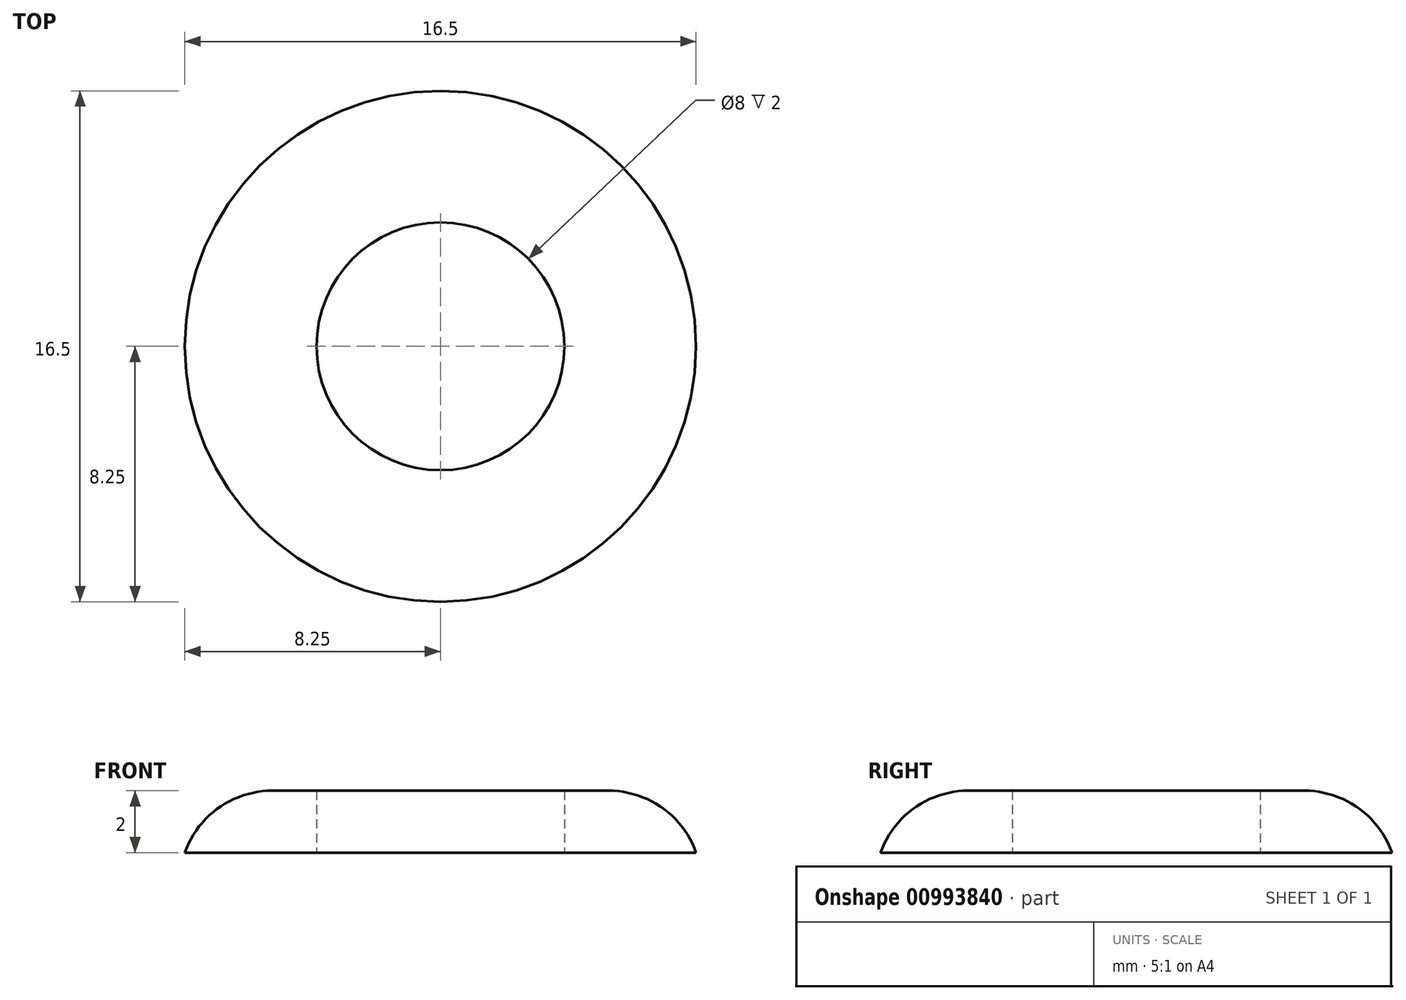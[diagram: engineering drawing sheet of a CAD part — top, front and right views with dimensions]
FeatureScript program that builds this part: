
annotation { "Feature Type Name" : "Feature", "Feature Type Description" : "" }
export const myFeature = defineFeature(function(context is Context, id is Id, definition is map)
    precondition{}
    {
        {
            var Q0;
            Q0=qCreatedBy(makeId("Top.planeOp"),FACE);
            var sketch = newSketch(context, id + "F0", { "sketchPlane" : qUnion([Q0])});
            skCircle(sketch, "E0", {"center": v(0, 0) * mm, "radius": 8.25 * mm});
            skCircle(sketch, "E1", {"center": v(0, 0) * mm, "radius": 4 * mm});
            skSolve(sketch);
        }
        {
            var Q0;
            Q0=makeQuery(id+"F0.imprint","IMPRINT",FACE,{"disambiguationData":[TD([[makeQuery(id+"F0.imprint","IMPRINT",EDGE,{"derivedFrom":sQuery(id+"F0.wireOp",EDGE,"E0")}),1.0]])]});
            var Q1;
            Q1=makeQuery(id+"F0.imprint","IMPRINT",FACE,{"disambiguationData":[TD([[makeQuery(id+"F0.imprint","IMPRINT",EDGE,{"derivedFrom":sQuery(id+"F0.wireOp",EDGE,"E1")}),1.0]])]});
            extrude(context, id + "F1", {"entities" : qUnion([Q0, Q1]), "depth" : 2 * mm, "offsetDistance" : 25 * mm});
        }
        {
            var Q0;
            Q0=makeQuery(id+"F0.imprint","IMPRINT",FACE,{"disambiguationData":[TD([[makeQuery(id+"F0.imprint","IMPRINT",EDGE,{"derivedFrom":sQuery(id+"F0.wireOp",EDGE,"E1")}),1.0]])]});
            var Q1;
            Q1=makeQuery(id+"F1.opExtrude","CAP_FACE",FACE,{"disambiguationData":[OSD([sQuery(id+"F0.wireOp",EDGE,"E0")])],"isStart":false});
            extrude(context, id + "F2", {"entities" : qUnion([Q0]), "operationType" : NewBodyOperationType.REMOVE, "endBound" : BoundingType.UP_TO_SURFACE, "depth" : 25 * mm, "endBoundEntityFace" : qUnion([Q1]), "offsetDistance" : 25 * mm});
        }
        {
            var Q0;
            Q0=makeQuery(id+"F1.opExtrude","CAP_EDGE",EDGE,{"disambiguationData":[OSD([sQuery(id+"F0.wireOp",EDGE,"E0")])],"isStart":false});
            fillet(context, id + "F3", {"entities" : qUnion([Q0]), "radius" : 3 * mm, "tangentPropagation" : true, "allowEdgeOverflow" : false});
        }
    });
